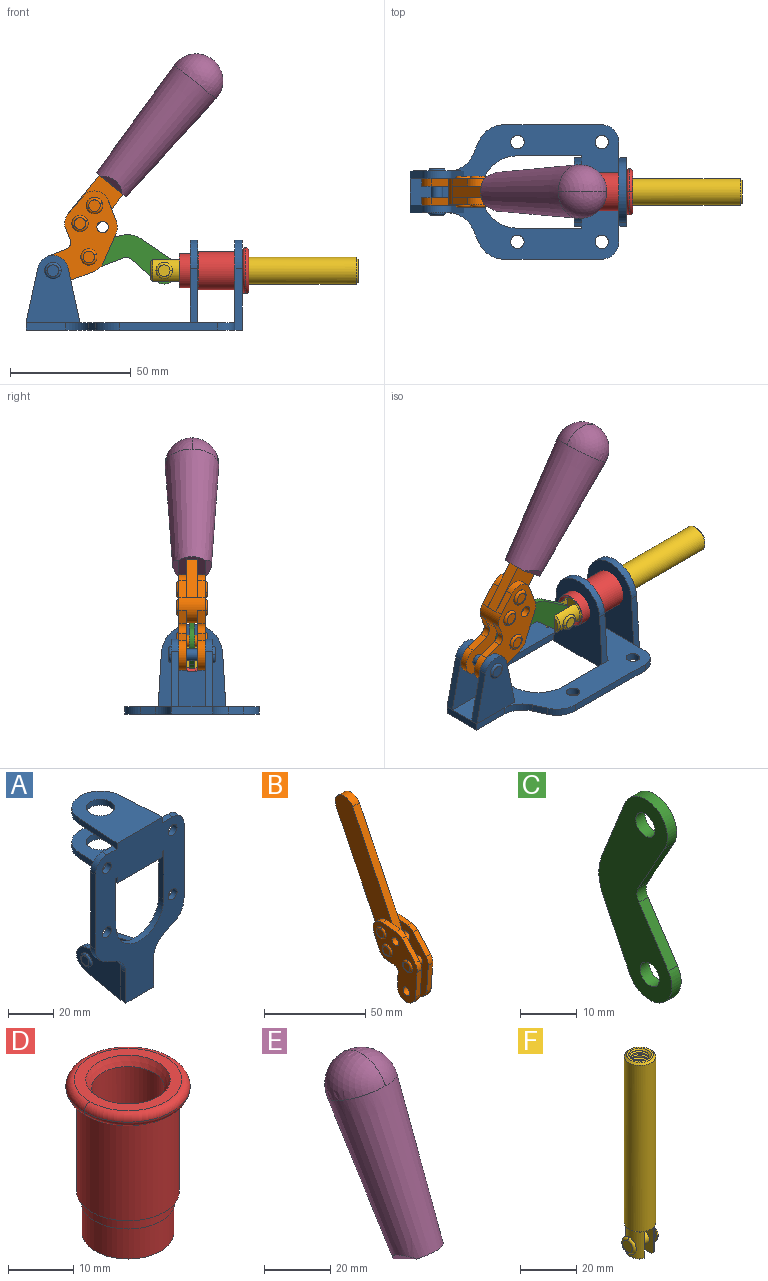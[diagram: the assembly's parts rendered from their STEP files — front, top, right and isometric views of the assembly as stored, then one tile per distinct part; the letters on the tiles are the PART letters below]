
ASSEMBLY  parts=6 mates=7
PART A: 55 faces, bbox 55.7x37.4x89.8 mm
  f0: torus R=2.41mm, axis (-1,0,0), area 15mm2, adj f11,f15,f25
  f1: torus R=2.41mm, axis (-1,0,0), area 15mm2, adj f10,f12,f22
  f2: cylinder r=2.78mm len=5.56mm, axis (0,-1,0), area 54.2mm2, adj f30,f54
  f3: cylinder r=14.99mm len=29.97mm, axis (0,-1,0), area 145.9mm2, adj f30,f49,f53,f54
  f4: cylinder r=2.78mm len=5.56mm, axis (0,-1,0), area 54.2mm2, adj f30,f54
  f5: cylinder r=2.78mm len=5.56mm, axis (0,-1,0), area 54.2mm2, adj f30,f54
  f6: cylinder r=2.78mm len=5.56mm, axis (0,-1,0), area 54.2mm2, adj f30,f54
  f7: cylinder r=6.35mm len=12.7mm, axis (0,0,1), area 123.6mm2, adj f27,f51
  f8: cylinder r=6.35mm len=12.7mm, axis (0,0,-1), area 124.7mm2, adj f21,f35
  f9: cylinder r=2.41mm len=11.18mm, axis (-1,0,0), area 169.4mm2, adj f16,f19
  f10: plane 4.83x4.83mm, normal (1,0,0), area 18.3mm2, adj f1,f12
  f11: plane 4.83x4.83mm, normal (-1,0,0), area 18.3mm2, adj f0,f15
  f12: torus R=2.41mm, axis (-1,0,0), area 15mm2, adj f1,f10,f22
  f13: cylinder r=6.35mm len=12.41mm, axis (1,0,0), area 53.4mm2, adj f18,f19,f22,f23
  f14: cylinder r=6.35mm len=12.41mm, axis (-1,0,0), area 53.4mm2, adj f16,f17,f24,f25
  f15: torus R=2.41mm, axis (-1,0,0), area 15mm2, adj f0,f11,f25
  f16: plane 27.86x22.35mm, normal (1,0,0), area 425.4mm2, adj f9,f14,f17,f24,f30
  f17: plane 22.86x4.97mm, normal (0,0.21,0.98), area 72.5mm2, adj f14,f16,f25,f30
  f18: plane 22.86x4.97mm, normal (0,0.21,0.98), area 72.5mm2, adj f13,f19,f22,f30
  f19: plane 27.86x22.35mm, normal (-1,0,0), area 425.4mm2, adj f9,f13,f18,f23,f30
  f20: cylinder r=12.7mm len=25.35mm, axis (0,0,-1), area 119.8mm2, adj f21,f34,f35,f36
  f21: plane 34.21x28.07mm, normal (0,0,-1), area 702.4mm2, adj f8,f20,f30,f34,f36
  f22: plane 27.96x22.45mm, normal (1,0,0), area 407.2mm2, adj f1,f12,f13,f18,f23,f30,f42,f43
  f23: plane 22.86x4.97mm, normal (0,0.21,-0.98), area 72.5mm2, adj f13,f19,f22,f44
  f24: plane 22.86x4.97mm, normal (0,0.21,-0.98), area 72.5mm2, adj f14,f16,f25,f44
  f25: plane 27.86x22.35mm, normal (-1,0,0), area 407.1mm2, adj f0,f14,f15,f17,f24,f30,f45,f46
  f26: plane 3.1x0.95mm, normal (0,0,-1), area 2.7mm2, adj f30,f49,f50,f54
  f27: plane 34.21x28.07mm, normal (0,0,1), area 702.4mm2, adj f7,f28,f30,f50,f52
  f28: cylinder r=12.7mm len=25.35mm, axis (0,0,1), area 118.8mm2, adj f27,f50,f51,f52
  f29: plane 3.1x0.95mm, normal (0,0,-1), area 2.7mm2, adj f30,f52,f53,f54
  f30: plane 86.54x55.63mm, normal (0,1,0), area 2362.9mm2, adj f2,f3,f4,f5,f6,f16,f17,f18
  f31: plane 40.56x3.1mm, normal (-1,0,0), area 125.7mm2, adj f30,f32,f48,f54
  f32: cylinder r=7.11mm len=7.11mm, axis (0,-1,0), area 34.6mm2, adj f30,f31,f33,f54
  f33: plane 6.67x3.1mm, normal (0,0,1), area 20.4mm2, adj f30,f32,f34,f54
  f34: plane 25.39x3.13mm, normal (-1,0.06,0), area 79.5mm2, adj f20,f21,f33,f35,f54
  f35: plane 37.31x28.45mm, normal (0,0,1), area 789.9mm2, adj f8,f20,f34,f36,f54
  f36: plane 25.39x3.13mm, normal (1,0.06,0), area 79.5mm2, adj f20,f21,f35,f37,f54
  f37: plane 6.67x3.1mm, normal (0,0,1), area 20.4mm2, adj f30,f36,f38,f54
  f38: cylinder r=7.11mm len=7.11mm, axis (0,-1,0), area 34.6mm2, adj f30,f37,f39,f54
  f39: plane 40.56x3.1mm, normal (1,0,0), area 125.7mm2, adj f30,f38,f40,f54
  f40: cylinder r=11.18mm len=10.16mm, axis (0,-1,0), area 39.5mm2, adj f30,f39,f41,f54
  f41: plane 6.09x3.1mm, normal (0.42,0,-0.91), area 20.8mm2, adj f30,f40,f42,f54
  f42: cylinder r=11.18mm len=9.41mm, axis (0,-1,0), area 37.2mm2, adj f22,f30,f41,f43,f54
  f43: plane 16.5x3.1mm, normal (1,0,0), area 51.1mm2, adj f22,f42,f44,f54
  f44: plane 17.37x3.1mm, normal (0,0,-1), area 53.8mm2, adj f23,f24,f30,f43,f45,f54
  f45: plane 16.5x3.1mm, normal (-1,0,0), area 51.1mm2, adj f25,f44,f46,f54
  f46: cylinder r=11.18mm len=9.41mm, axis (0,-1,0), area 37.2mm2, adj f25,f30,f45,f47,f54
  f47: plane 6.09x3.1mm, normal (-0.42,0,-0.91), area 20.8mm2, adj f30,f46,f48,f54
  f48: cylinder r=11.18mm len=10.16mm, axis (0,-1,0), area 39.5mm2, adj f30,f31,f47,f54
  f49: plane 26.54x3.1mm, normal (-1,0,0), area 82.3mm2, adj f3,f26,f30,f54
  f50: plane 25.39x3.1mm, normal (1,0.06,0), area 78.8mm2, adj f26,f27,f28,f51,f54
  f51: plane 37.31x28.45mm, normal (0,0,-1), area 789.9mm2, adj f7,f28,f50,f52,f54
  f52: plane 25.39x3.1mm, normal (-1,0.06,0), area 78.8mm2, adj f27,f28,f29,f51,f54
  f53: plane 26.54x3.1mm, normal (1,0,0), area 82.3mm2, adj f3,f29,f30,f54
  f54: plane 89.66x55.63mm, normal (0,-1,0), area 2678.5mm2, adj f2,f3,f4,f5,f6,f26,f29,f31
PART B: 59 faces, bbox 12.9x60.2x99.6 mm
  f0: torus R=2.39mm, axis (-1,0,0), area 14.9mm2, adj f20,f43,f51
  f1: torus R=2.39mm, axis (-1,0,0), area 14.9mm2, adj f19,f42,f51
  f2: torus R=2.39mm, axis (-1,0,0), area 14.9mm2, adj f18,f35,f51
  f3: torus R=2.39mm, axis (-1,0,0), area 14.9mm2, adj f14,f17,f23
  f4: torus R=2.39mm, axis (-1,0,0), area 14.9mm2, adj f13,f16,f23
  f5: torus R=2.39mm, axis (-1,0,0), area 14.9mm2, adj f12,f15,f23
  f6: cylinder r=2.39mm len=4.78mm, axis (1,0,0), area 46.5mm2, adj f48,f50,f51
  f7: cylinder r=2.39mm len=4.78mm, axis (1,0,0), area 46.5mm2, adj f50,f51
  f8: cylinder r=6.35mm len=12.68mm, axis (1,0,0), area 61.8mm2, adj f38,f39,f50,f51
  f9: cylinder r=2.39mm len=4.78mm, axis (-1,0,0), area 70.5mm2, adj f46,f50
  f10: cylinder r=2.39mm len=4.78mm, axis (-1,0,0), area 46.5mm2, adj f23,f45,f46
  f11: cylinder r=2.39mm len=4.78mm, axis (-1,0,0), area 46.5mm2, adj f23,f46
  f12: plane 4.78x4.78mm, normal (1,0,0), area 17.9mm2, adj f5,f15
  f13: plane 4.78x4.78mm, normal (1,0,0), area 17.9mm2, adj f4,f16
  f14: plane 4.78x4.78mm, normal (1,0,0), area 17.9mm2, adj f3,f17
  f15: torus R=2.39mm, axis (-1,0,0), area 14.9mm2, adj f5,f12,f23
  f16: torus R=2.39mm, axis (-1,0,0), area 14.9mm2, adj f4,f13,f23
  f17: torus R=2.39mm, axis (-1,0,0), area 14.9mm2, adj f3,f14,f23
  f18: plane 4.78x4.78mm, normal (-1,0,0), area 17.9mm2, adj f2,f35
  f19: plane 4.78x4.78mm, normal (-1,0,0), area 17.9mm2, adj f1,f42
  f20: plane 4.78x4.78mm, normal (-1,0,0), area 17.9mm2, adj f0,f43
  f21: plane 2.26x0.2mm, normal (1,0,0), area 0.2mm2, adj f31,f44
  f22: plane 2.26x0.2mm, normal (-1,0,0), area 0.2mm2, adj f41,f44
  f23: plane 39.37x30.77mm, normal (1,0,0), area 565.5mm2, adj f3,f4,f5,f10,f11,f15,f16,f17
  f24: cylinder r=6.1mm len=4.15mm, axis (-1,0,0), area 14.7mm2, adj f23,f25,f32,f46
  f25: plane 10.25x9.01mm, normal (0,-0.75,0.66), area 42.3mm2, adj f23,f24,f26,f46
  f26: cylinder r=6.35mm len=4.64mm, axis (-1,0,0), area 15.6mm2, adj f23,f25,f27,f46
  f27: plane 15.84x3.1mm, normal (0,-1,-0.07), area 49.2mm2, adj f23,f26,f28,f46
  f28: cylinder r=6.35mm len=12.68mm, axis (-1,0,0), area 61.8mm2, adj f23,f27,f29,f46
  f29: plane 8.11x3.1mm, normal (0,1,0.07), area 25.2mm2, adj f23,f28,f30,f46
  f30: cylinder r=3.05mm len=3.25mm, axis (-1,0,0), area 14.8mm2, adj f23,f29,f31,f46
  f31: plane 5.99x3.1mm, normal (0,0.07,-1), area 18.6mm2, adj f21,f23,f30,f44,f46
  f32: plane 9.5x3.1mm, normal (0,-0.07,1), area 29.5mm2, adj f23,f24,f33,f46,f47
  f33: cylinder r=6.1mm len=8.63mm, axis (-1,0,0), area 39.1mm2, adj f23,f32,f34,f47
  f34: plane 8.65x3.96mm, normal (0,0.91,-0.42), area 29.5mm2, adj f23,f33,f44,f47
  f35: torus R=2.39mm, axis (-1,0,0), area 14.9mm2, adj f2,f18,f51
  f36: plane 10.25x9.01mm, normal (0,-0.75,0.66), area 42.3mm2, adj f37,f49,f50,f51
  f37: cylinder r=6.35mm len=4.64mm, axis (1,0,0), area 15.6mm2, adj f36,f38,f50,f51
  f38: plane 15.84x3.1mm, normal (0,-1,-0.07), area 49.2mm2, adj f8,f37,f50,f51
  f39: plane 8.11x3.1mm, normal (0,1,0.07), area 25.2mm2, adj f8,f40,f50,f51
  f40: cylinder r=3.05mm len=3.25mm, axis (1,0,0), area 14.8mm2, adj f39,f41,f50,f51
  f41: plane 5.99x3.1mm, normal (0,0.07,-1), area 18.6mm2, adj f22,f40,f44,f50,f51
  f42: torus R=2.39mm, axis (-1,0,0), area 14.9mm2, adj f1,f19,f51
  f43: torus R=2.39mm, axis (-1,0,0), area 14.9mm2, adj f0,f20,f51
  f44: cylinder r=6.35mm len=12.12mm, axis (-1,0,0), area 128.9mm2, adj f21,f22,f23,f31,f34,f41,f46,f47
  f45: plane 2.65x1.35mm, normal (1,0,0), area 1mm2, adj f10,f55
  f46: plane 39.08x20.42mm, normal (-1,0,0), area 412.5mm2, adj f9,f10,f11,f24,f25,f26,f27,f28
  f47: plane 77.62x39.82mm, normal (1,0,0), area 850mm2, adj f32,f33,f34,f44,f53,f54,f55
  f48: plane 2.65x1.35mm, normal (-1,0,0), area 1mm2, adj f6,f55
  f49: cylinder r=6.1mm len=4.15mm, axis (1,0,0), area 14.7mm2, adj f36,f50,f51,f56
  f50: plane 39.08x20.42mm, normal (1,0,0), area 412.5mm2, adj f6,f7,f8,f9,f36,f37,f38,f39
  f51: plane 39.37x30.77mm, normal (-1,0,0), area 565.5mm2, adj f0,f1,f2,f6,f7,f8,f35,f36
  f52: plane 8.65x3.96mm, normal (0,0.91,-0.42), area 29.5mm2, adj f44,f51,f57,f58
  f53: plane 68.49x33.4mm, normal (0,0.9,-0.44), area 358.1mm2, adj f44,f47,f54,f58
  f54: cylinder r=6.35mm len=12.06mm, axis (1,0,0), area 93.7mm2, adj f47,f53,f55,f58
  f55: plane 68.49x33.4mm, normal (0,-0.9,0.44), area 358.1mm2, adj f44,f45,f46,f47,f48,f50,f54,f58
  f56: plane 9.5x3.1mm, normal (0,-0.07,1), area 29.5mm2, adj f49,f50,f51,f57,f58
  f57: cylinder r=6.1mm len=8.63mm, axis (1,0,0), area 39.1mm2, adj f51,f52,f56,f58
  f58: plane 77.62x39.82mm, normal (-1,0,0), area 850mm2, adj f44,f52,f53,f54,f55,f56,f57
PART C: 12 faces, bbox 2.3x18.2x42.8 mm
  f0: cylinder r=2.4mm len=4.8mm, axis (1,0,0), area 34.9mm2, adj f4,f11
  f1: cylinder r=10.41mm len=8.47mm, axis (1,0,0), area 20.2mm2, adj f4,f9,f10,f11
  f2: cylinder r=3.05mm len=3.16mm, axis (1,0,0), area 7.7mm2, adj f4,f6,f7,f11
  f3: cylinder r=2.4mm len=4.8mm, axis (1,0,0), area 34.9mm2, adj f4,f11
  f4: plane 42.81x18.23mm, normal (-1,0,0), area 414.1mm2, adj f0,f1,f2,f3,f5,f6,f7,f8
  f5: cylinder r=5.54mm len=10.67mm, axis (1,0,0), area 41.8mm2, adj f4,f6,f10,f11
  f6: plane 11.66x6.53mm, normal (0,-0.87,-0.49), area 30.9mm2, adj f2,f4,f5,f11
  f7: plane 11.17x7.33mm, normal (0,-0.84,0.55), area 30.9mm2, adj f2,f4,f8,f11
  f8: cylinder r=5.54mm len=10.51mm, axis (1,0,0), area 41.8mm2, adj f4,f7,f9,f11
  f9: plane 13.67x6.67mm, normal (0,0.9,-0.44), area 35.1mm2, adj f1,f4,f8,f11
  f10: plane 14.1x5.7mm, normal (0,0.93,0.37), area 35.1mm2, adj f1,f4,f5,f11
  f11: plane 42.81x18.23mm, normal (1,0,0), area 414.1mm2, adj f0,f1,f2,f3,f5,f6,f7,f8
PART D: 15 faces, bbox 20.6x20.6x28.7 mm
  f0: torus R=8.26mm, axis (0,0,1), area 56.8mm2, adj f1,f10,f12
  f1: torus R=8.26mm, axis (0,0,1), area 56.8mm2, adj f0,f6,f13
  f2: cylinder r=5.59mm len=25.91mm, axis (0,0,1), area 909.6mm2, adj f3,f4
  f3: cone r=6.86mm half-angle=45deg, axis (0,0,-1), area 70.2mm2, adj f2,f14
  f4: cone r=6.47mm half-angle=30deg, axis (0,0,1), area 66.7mm2, adj f2,f13
  f5: cylinder r=7.04mm len=14.07mm, axis (0,0,1), area 252.6mm2, adj f11,f14
  f6: torus R=8.26mm, axis (0,0,1), area 56.8mm2, adj f1,f12,f13
  f7: cylinder r=7.16mm len=14.33mm, axis (0,0,1), area 91.5mm2, adj f9,f11
  f8: cylinder r=7.86mm len=18.42mm, axis (0,0,1), area 909.6mm2, adj f9,f10
  f9: plane 15.72x15.72mm, normal (0,0,-1), area 33mm2, adj f7,f8
  f10: plane 16.51x16.51mm, normal (0,0,-1), area 19.9mm2, adj f0,f8,f12
  f11: plane 14.33x14.33mm, normal (0,0,-1), area 5.7mm2, adj f5,f7
  f12: torus R=8.26mm, axis (0,0,1), area 56.8mm2, adj f0,f6,f10
  f13: plane 16.51x16.51mm, normal (0,0,1), area 82.7mm2, adj f1,f4,f6
  f14: plane 14.07x14.07mm, normal (0,0,-1), area 7.8mm2, adj f3,f5
PART E: 11 faces, bbox 22.3x42.6x64.5 mm
  f0: sphere r=11.13mm, area 411.4mm2, adj f1,f8
  f1: cone r=11.11mm half-angle=3.3deg, axis (0,0.44,0.9), area 3251.8mm2, adj f0,f7,f8,f9,f10
  f2: cylinder r=6.16mm len=11.7mm, axis (1,0,0), area 89.5mm2, adj f3,f4,f5,f6
  f3: plane 60.23x36.75mm, normal (-1,0,0), area 763.6mm2, adj f2,f4,f6,f10
  f4: plane 51.37x25.05mm, normal (0,0.9,-0.44), area 264.2mm2, adj f2,f3,f5,f10
  f5: plane 60.23x36.75mm, normal (1,0,0), area 763.6mm2, adj f2,f4,f6,f10
  f6: plane 51.37x25.05mm, normal (0,-0.9,0.44), area 264.2mm2, adj f2,f3,f5,f10
  f7: plane 9.95x5.95mm, normal (0.71,-0.31,-0.64), area 25.8mm2, adj f1,f10
  f8: sphere r=11.13mm, area 411.4mm2, adj f0,f1
  f9: plane 9.95x5.95mm, normal (-0.71,-0.31,-0.64), area 25.8mm2, adj f1,f10
  f10: plane 14.27x11.38mm, normal (0,-0.44,-0.9), area 106.7mm2, adj f1,f3,f4,f5,f6,f7,f9
PART F: 48 faces, bbox 12.6x11.1x86.1 mm
  f0: torus R=2.41mm, axis (-1,0,0), area 15mm2, adj f30,f32,f34
  f1: torus R=2.41mm, axis (-1,0,0), area 15mm2, adj f29,f31,f33
  f2: cylinder r=5.54mm len=72.39mm, axis (0,0,1), area 2518.5mm2, adj f3,f4,f42,f43
  f3: cone r=5.54mm half-angle=45deg, axis (0,0,1), area 7.6mm2, adj f2,f5,f41
  f4: cone r=5.54mm half-angle=45deg, axis (0,0,-1), area 34.9mm2, adj f2,f39
  f5: cylinder r=5.08mm len=11.48mm, axis (0,0,1), area 108.3mm2, adj f3,f7,f8,f41
  f6: cylinder r=2.41mm len=4.83mm, axis (-1,0,0), area 71.2mm2, adj f40,f41
  f7: cylinder r=2.41mm len=4.83mm, axis (-1,0,0), area 7.6mm2, adj f5,f34
  f8: cone r=5.08mm half-angle=45deg, axis (0,0,1), area 10.6mm2, adj f5,f37,f41
  f9: cone r=3.98mm half-angle=45deg, axis (0,0,1), area 17.6mm2, adj f27,f39,f45,f46,f47
  f10: cylinder r=2.41mm len=4.83mm, axis (-1,0,0), area 7.6mm2, adj f33,f38
  f11: cylinder r=3.2mm len=6.4mm, axis (0,0,1), area 78.4mm2, adj f12,f28,f44,f45,f47
  f12: cylinder r=3.2mm len=6.4mm, axis (0,0,1), area 10.5mm2, adj f11,f13,f45,f47
  f13: cylinder r=3.2mm len=6.4mm, axis (0,0,1), area 10.5mm2, adj f12,f14,f45,f47
  f14: cylinder r=3.2mm len=6.4mm, axis (0,0,1), area 10.5mm2, adj f13,f15,f45,f47
  f15: cylinder r=3.2mm len=6.4mm, axis (0,0,1), area 10.5mm2, adj f14,f16,f45,f47
  f16: cylinder r=3.2mm len=6.4mm, axis (0,0,1), area 10.5mm2, adj f15,f17,f45,f47
  f17: cylinder r=3.2mm len=6.4mm, axis (0,0,1), area 10.5mm2, adj f16,f18,f45,f47
  f18: cylinder r=3.2mm len=6.4mm, axis (0,0,1), area 10.5mm2, adj f17,f19,f45,f47
  f19: cylinder r=3.2mm len=6.4mm, axis (0,0,1), area 10.5mm2, adj f18,f20,f45,f47
  f20: cylinder r=3.2mm len=6.4mm, axis (0,0,1), area 10.5mm2, adj f19,f21,f45,f47
  f21: cylinder r=3.2mm len=6.4mm, axis (0,0,1), area 10.5mm2, adj f20,f22,f45,f47
  f22: cylinder r=3.2mm len=6.4mm, axis (0,0,1), area 10.5mm2, adj f21,f23,f45,f47
  f23: cylinder r=3.2mm len=6.4mm, axis (0,0,1), area 10.5mm2, adj f22,f24,f45,f47
  f24: cylinder r=3.2mm len=6.4mm, axis (0,0,1), area 10.5mm2, adj f23,f25,f45,f47
  f25: cylinder r=3.2mm len=6.4mm, axis (0,0,1), area 10.5mm2, adj f24,f26,f45,f47
  f26: cylinder r=3.2mm len=6.4mm, axis (0,0,1), area 10.5mm2, adj f25,f27,f45,f47
  f27: cylinder r=3.2mm len=6.4mm, axis (0,0,1), area 7.4mm2, adj f9,f26,f45,f47
  f28: cone r=3.2mm half-angle=60deg, axis (0,0,1), area 37.2mm2, adj f11
  f29: plane 4.83x4.83mm, normal (-1,0,0), area 18.3mm2, adj f1,f31
  f30: plane 4.83x4.83mm, normal (1,0,0), area 18.3mm2, adj f0,f32
  f31: torus R=2.41mm, axis (-1,0,0), area 15mm2, adj f1,f29,f33
  f32: torus R=2.41mm, axis (-1,0,0), area 15mm2, adj f0,f30,f34
  f33: plane 6.83x6.83mm, normal (1,0,0), area 18.3mm2, adj f1,f10,f31
  f34: plane 6.83x6.83mm, normal (-1,0,0), area 18.3mm2, adj f0,f7,f32
  f35: cone r=5.08mm half-angle=45deg, axis (0,0,1), area 10.6mm2, adj f36,f38,f40
  f36: plane 7.25x1.97mm, normal (0,0,-1), area 10mm2, adj f35,f40
  f37: plane 7.25x1.97mm, normal (0,0,-1), area 10mm2, adj f8,f41
  f38: cylinder r=5.08mm len=11.48mm, axis (0,0,1), area 108.3mm2, adj f10,f35,f40,f42
  f39: plane 9.55x9.55mm, normal (0,0,1), area 22mm2, adj f4,f9
  f40: plane 12.76x10.09mm, normal (1,0,0), area 95.7mm2, adj f6,f35,f36,f38,f42,f43
  f41: plane 12.76x10.09mm, normal (-1,0,0), area 95.7mm2, adj f3,f5,f6,f8,f37,f43
  f42: cone r=5.54mm half-angle=45deg, axis (0,0,1), area 7.6mm2, adj f2,f38,f40
  f43: plane 11.07x4.7mm, normal (0,0,-1), area 50.4mm2, adj f2,f40,f41
  f44: plane 0.89x0.62mm, normal (-1,0,0), area 0.3mm2, adj f11,f45,f46,f47
  f45: bspline ~24.8x7.63mm, area 266.6mm2, adj f9,f11,f12,f13,f14,f15,f16,f17
  f46: bspline ~24.87x7.63mm, area 73.6mm2, adj f9,f44,f45,f47
  f47: bspline ~24.98x7.63mm, area 272.5mm2, adj f9,f11,f12,f13,f14,f15,f16,f17
PLACE A rot(axis=(0.58,0.58,0.58),120deg) t=(0,0,0)mm fixed
PLACE B rot(axis=(0.47,0.47,0.74),106.8deg) t=(7.38,0,15.8)mm
PLACE C rot(axis=(0.61,0.61,0.5),127.3deg) t=(-6.37,0,3.85)mm
PLACE D rot(axis=(0.71,0,0.71),180deg) t=(0,24.61,24.61)mm
PLACE E rot(axis=(-0.11,0.11,-0.99),90.7deg) t=(-53.44,0,67.3)mm
PLACE F rot(axis=(-0.58,0.58,-0.58),120deg) t=(-1.49,0,49.23)mm
MATE fastened D.f2 <-> A.f7  axis (-1,0,0) through (46.39,0,24.61)mm
MATE revolute B.f4 <-> C.f3  axis (0,-1,0) through (-17.26,0,30.27)mm
MATE parallel D.f0 <-> F.f2  axis (-1,0,0) through (20.23,0,24.61)mm
MATE revolute B.f7 <-> A.f0  axis (0,-1,0) through (-32.09,0,24.61)mm
MATE revolute F.f6 <-> C.f5  axis (0,1,0) through (13.98,0,24.61)mm
MATE slider F.f2 <-> D.f2  axis (1,0,0) through (57.29,0,24.61)mm
MATE fastened E.f0 <-> B.f54  axis (0,1,0) through (27.16,0,103.29)mm
